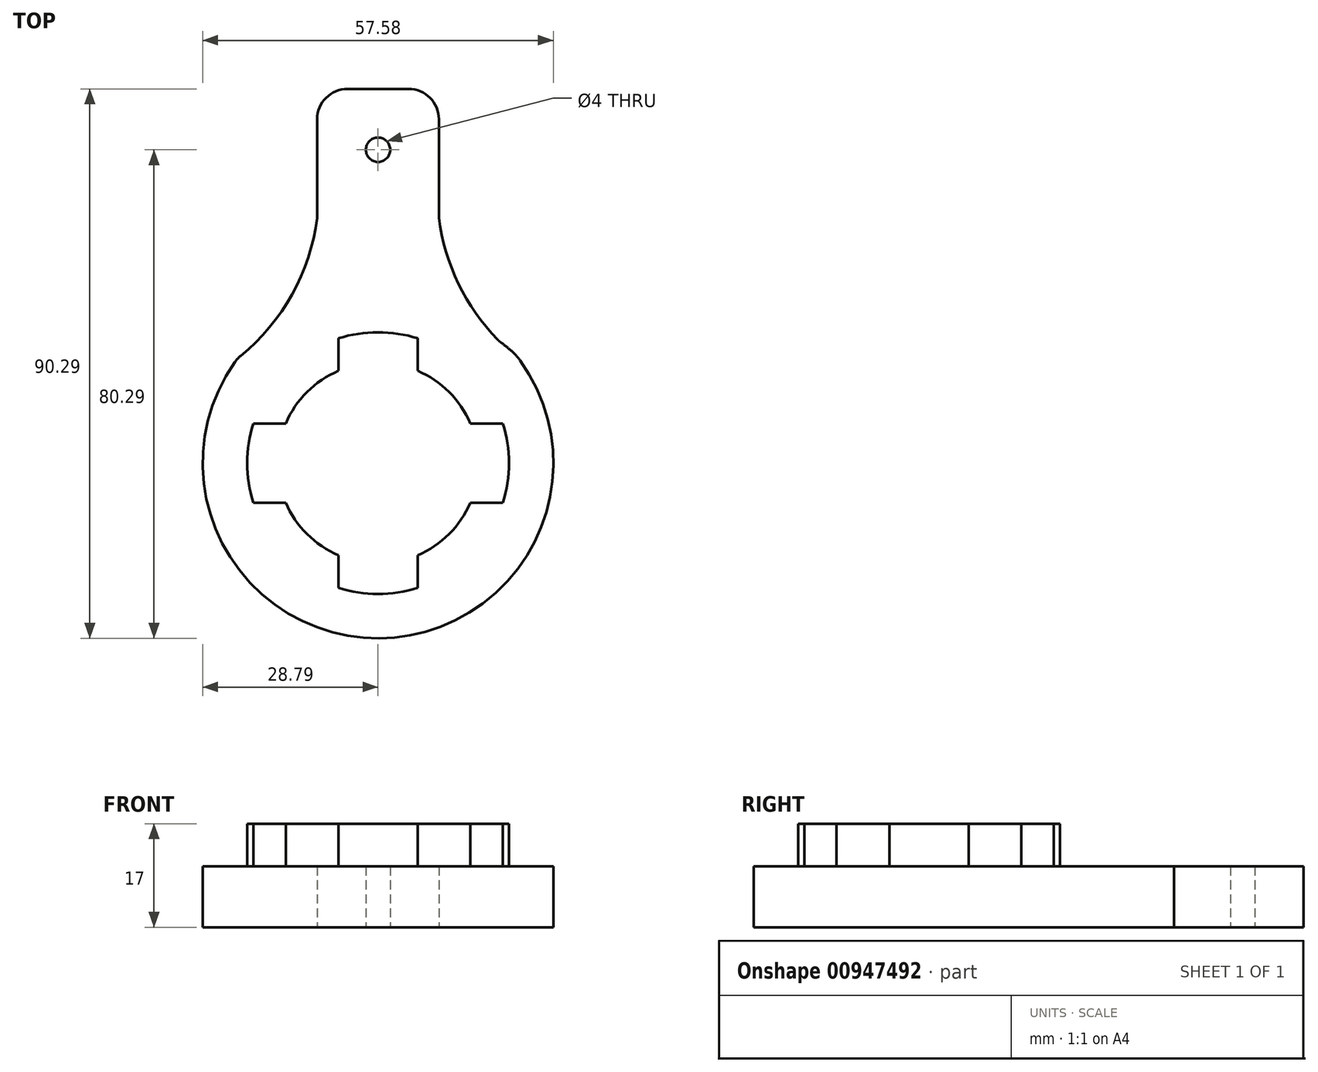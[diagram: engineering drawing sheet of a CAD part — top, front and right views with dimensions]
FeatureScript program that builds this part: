
annotation { "Feature Type Name" : "Feature", "Feature Type Description" : "" }
export const myFeature = defineFeature(function(context is Context, id is Id, definition is map)
    precondition{}
    {
        {
            var Q0;
            Q0=qCreatedBy(makeId("Top.planeOp"),FACE);
            var sketch = newSketch(context, id + "F0", { "sketchPlane" : qUnion([Q0])});
            skCircle(sketch, "E0", {"center": v(0, 0) * mm, "radius": 21.5 * mm});
            skCircle(sketch, "E1", {"center": v(0, 0) * mm, "radius": 16.5 * mm});
            skLineSegment(sketch, "E2", {"start": v(-6.5, 15.17) * mm, "end": v(-6.5, 20.5) * mm});
            skLineSegment(sketch, "E3", {"start": v(6.5, 15.17) * mm, "end": v(6.5, 20.5) * mm});
            skLineSegment(sketch, "E4", {"start": v(15.17, 6.5) * mm, "end": v(20.5, 6.5) * mm});
            skLineSegment(sketch, "E5", {"start": v(15.17, -6.5) * mm, "end": v(20.5, -6.5) * mm});
            skLineSegment(sketch, "E6", {"start": v(-15.17, 6.5) * mm, "end": v(-20.5, 6.5) * mm});
            skLineSegment(sketch, "E7", {"start": v(-15.17, -6.5) * mm, "end": v(-20.5, -6.5) * mm});
            skLineSegment(sketch, "E8", {"start": v(-6.5, -15.17) * mm, "end": v(-6.5, -20.5) * mm});
            skLineSegment(sketch, "E9", {"start": v(6.5, -15.17) * mm, "end": v(6.5, -20.5) * mm});
            skLineSegment(sketch, "E10", {"start": v(0, 61.5) * mm, "end": v(10, 61.5) * mm});
            skLineSegment(sketch, "E11", {"start": v(0, 61.5) * mm, "end": v(-10, 61.5) * mm});
            skLineSegment(sketch, "E12", {"start": v(-10, 61.5) * mm, "end": v(-10, 19.03) * mm});
            skLineSegment(sketch, "E13", {"start": v(10, 61.5) * mm, "end": v(10, 19.03) * mm});
            skArc(sketch, "E14", {"start": v(-23, 17.26) * mm, "mid": v(-14.25, 27.49) * mm, "end": v(-10, 40.27) * mm});
            skArc(sketch, "E15", {"start": v(10, 40.27) * mm, "mid": v(13.3, 29.29) * mm, "end": v(19.97, 19.97) * mm});
            skArc(sketch, "E16", {"start": v(-23, 17.26) * mm, "mid": v(-23.09, 17.18) * mm, "end": v(-23.16, 17.1) * mm});
            skArc(sketch, "E17", {"start": v(-23.16, 17.1) * mm, "mid": v(0.44, -28.79) * mm, "end": v(22.63, 17.8) * mm});
            skArc(sketch, "E18.trimOffspring", {"start": v(17.2, 23.09) * mm, "mid": v(0, 28.79) * mm, "end": v(-17.2, 23.09) * mm});
            skArc(sketch, "E19.trimOffspring", {"start": v(22.63, 17.8) * mm, "mid": v(21.34, 18.93) * mm, "end": v(19.97, 19.97) * mm});
            skLineSegment(sketch, "E20", {"start": v(0, 61.5) * mm, "end": v(0, 51.5) * mm});
            skSolve(sketch);
        }
        {
            var Q0;
            {var subQ0=sQuery(id+"F0.wireOp",EDGE,"E16");Q0=makeQuery(id+"F0.imprint","IMPRINT",FACE,{"disambiguationData":[TD([[makeQuery(id+"F0.imprint","IMPRINT",EDGE,{"derivedFrom":subQ0}),1.0]])]});}
            var Q1;
            {var subQ0=sQuery(id+"F0.wireOp",EDGE,"E2");Q1=makeQuery(id+"F0.imprint","IMPRINT",FACE,{"disambiguationData":[TD([[makeQuery(id+"F0.imprint","IMPRINT",EDGE,{"derivedFrom":subQ0}),1.0]])]});}
            var Q2;
            {var subQ0=sQuery(id+"F0.wireOp",EDGE,"E3");Q2=makeQuery(id+"F0.imprint","IMPRINT",FACE,{"disambiguationData":[TD([[makeQuery(id+"F0.imprint","IMPRINT",EDGE,{"derivedFrom":subQ0}),-1.0]])]});}
            var Q3;
            {var subQ0=sQuery(id+"F0.wireOp",EDGE,"E7");Q3=makeQuery(id+"F0.imprint","IMPRINT",FACE,{"disambiguationData":[TD([[makeQuery(id+"F0.imprint","IMPRINT",EDGE,{"derivedFrom":subQ0}),1.0]])]});}
            var Q4;
            {var subQ0=sQuery(id+"F0.wireOp",EDGE,"E5");Q4=makeQuery(id+"F0.imprint","IMPRINT",FACE,{"disambiguationData":[TD([[makeQuery(id+"F0.imprint","IMPRINT",EDGE,{"derivedFrom":subQ0}),-1.0]])]});}
            var Q5;
            {var subQ1=sQuery(id+"F0.wireOp",EDGE,"E0");var subQ8=makeQuery(id+"F0.imprint","INTERSECT",VERTEX,{"derivedFrom":[subQ1,sQuery(id+"F0.wireOp",EDGE,"E3")]});Q5=makeQuery(id+"F0.imprint","IMPRINT",FACE,{"disambiguationData":[TD([[makeQuery(id+"F0.imprint","IMPRINT",EDGE,{"disambiguationData":[TD([[subQ8,1.0]])],"derivedFrom":subQ1}),-1.0]])]});}
            var Q6;
            {var subQ0=sQuery(id+"F0.wireOp",EDGE,"E15");var subQ1=sQuery(id+"F0.wireOp",EDGE,"E13");var subQ2=makeQuery(id+"F0.imprint","INTERSECT",VERTEX,{"derivedFrom":[subQ1,subQ0]});Q6=makeQuery(id+"F0.imprint","IMPRINT",FACE,{"disambiguationData":[TD([[makeQuery(id+"F0.imprint","IMPRINT",EDGE,{"disambiguationData":[TD([[subQ2,-1.0]])],"derivedFrom":subQ1}),1.0]])]});}
            var Q7;
            {var subQ0=sQuery(id+"F0.wireOp",EDGE,"E14");var subQ1=sQuery(id+"F0.wireOp",EDGE,"E12");var subQ2=makeQuery(id+"F0.imprint","INTERSECT",VERTEX,{"derivedFrom":[subQ1,subQ0]});Q7=makeQuery(id+"F0.imprint","IMPRINT",FACE,{"disambiguationData":[TD([[makeQuery(id+"F0.imprint","IMPRINT",EDGE,{"disambiguationData":[TD([[subQ2,-1.0]])],"derivedFrom":subQ1}),-1.0]])]});}
            var Q8;
            {var subQ5=sQuery(id+"F0.wireOp",EDGE,"E10");Q8=makeQuery(id+"F0.imprint","IMPRINT",FACE,{"disambiguationData":[TD([[makeQuery(id+"F0.imprint","IMPRINT",EDGE,{"derivedFrom":subQ5}),-1.0]])]});}
            extrude(context, id + "F1", {"entities" : qUnion([Q0, Q1, Q2, Q3, Q4, Q5, Q6, Q7, Q8]), "depth" : 10 * mm, "offsetDistance" : 25 * mm});
        }
        {
            var Q0;
            {var subQ0=sQuery(id+"F0.wireOp",EDGE,"E6");Q0=makeQuery(id+"F0.imprint","IMPRINT",FACE,{"disambiguationData":[TD([[makeQuery(id+"F0.imprint","IMPRINT",EDGE,{"derivedFrom":subQ0}),1.0]])]});}
            var Q1;
            {var subQ0=sQuery(id+"F0.wireOp",EDGE,"E1");var subQ4=makeQuery(id+"F0.imprint","INTERSECT",VERTEX,{"derivedFrom":[subQ0,sQuery(id+"F0.wireOp",EDGE,"E3")]});Q1=makeQuery(id+"F0.imprint","IMPRINT",FACE,{"disambiguationData":[TD([[makeQuery(id+"F0.imprint","IMPRINT",EDGE,{"disambiguationData":[TD([[subQ4,1.0]])],"derivedFrom":subQ0}),1.0]])]});}
            var Q2;
            {var subQ0=sQuery(id+"F0.wireOp",EDGE,"E2");Q2=makeQuery(id+"F0.imprint","IMPRINT",FACE,{"disambiguationData":[TD([[makeQuery(id+"F0.imprint","IMPRINT",EDGE,{"derivedFrom":subQ0}),-1.0]])]});}
            var Q3;
            {var subQ0=sQuery(id+"F0.wireOp",EDGE,"E4");Q3=makeQuery(id+"F0.imprint","IMPRINT",FACE,{"disambiguationData":[TD([[makeQuery(id+"F0.imprint","IMPRINT",EDGE,{"derivedFrom":subQ0}),-1.0]])]});}
            var Q4;
            {var subQ0=sQuery(id+"F0.wireOp",EDGE,"E8");Q4=makeQuery(id+"F0.imprint","IMPRINT",FACE,{"disambiguationData":[TD([[makeQuery(id+"F0.imprint","IMPRINT",EDGE,{"derivedFrom":subQ0}),1.0]])]});}
            extrude(context, id + "F2", {"entities" : qUnion([Q0, Q1, Q2, Q3, Q4]), "operationType" : NewBodyOperationType.ADD, "depth" : 17 * mm, "offsetDistance" : 25 * mm});
        }
        {
            var Q0;
            Q0=makeQuery(id+"F1.opExtrude","SWEPT_EDGE",EDGE,{"disambiguationData":[OSD([sQuery(id+"F0.wireOp",EDGE,"E11"),sQuery(id+"F0.wireOp",EDGE,"E12")])]});
            var Q1;
            Q1=makeQuery(id+"F1.opExtrude","SWEPT_EDGE",EDGE,{"disambiguationData":[OSD([sQuery(id+"F0.wireOp",EDGE,"E10"),sQuery(id+"F0.wireOp",EDGE,"E13")])]});
            fillet(context, id + "F3", {"entities" : qUnion([Q0, Q1]), "radius" : 5 * mm, "tangentPropagation" : true, "allowEdgeOverflow" : false});
        }
        {
            var Q0;
            Q0=sQuery(id+"F0.wireOp",VERTEX,"E20.end");
            var Q1;
            Q1=makeQuery(id+"F1.opExtrude","SWEPT_BODY",BODY,{"disambiguationData":[OSD([sQuery(id+"F0.wireOp",EDGE,"E0"),sQuery(id+"F0.wireOp",EDGE,"E1"),sQuery(id+"F0.wireOp",EDGE,"E2"),sQuery(id+"F0.wireOp",EDGE,"E3"),sQuery(id+"F0.wireOp",EDGE,"E4"),sQuery(id+"F0.wireOp",EDGE,"E5"),sQuery(id+"F0.wireOp",EDGE,"E6"),sQuery(id+"F0.wireOp",EDGE,"E7"),sQuery(id+"F0.wireOp",EDGE,"E8"),sQuery(id+"F0.wireOp",EDGE,"E9"),sQuery(id+"F0.wireOp",EDGE,"E10"),sQuery(id+"F0.wireOp",EDGE,"E11"),sQuery(id+"F0.wireOp",EDGE,"E12"),sQuery(id+"F0.wireOp",EDGE,"E13"),sQuery(id+"F0.wireOp",EDGE,"E14"),sQuery(id+"F0.wireOp",EDGE,"E15"),sQuery(id+"F0.wireOp",EDGE,"E16"),sQuery(id+"F0.wireOp",EDGE,"E17"),sQuery(id+"F0.wireOp",EDGE,"E19.trimOffspring")])]});
            hole(context, id + "F4", {"style" : HoleStyle.SIMPLE, "endStyle" : HoleEndStyle.THROUGH, "oppositeDirection" : true, "holeDiameter" : 4 * mm, "majorDiameter" : 5 * mm, "isTappedThrough" : true, "tappedDepth" : 12 * mm, "tapClearance" : 3, "locations" : qUnion([Q0]), "scope" : qUnion([Q1])});
        }
        {
            var Q0;
            Q0=makeQuery(id+"F1.opExtrude","SWEPT_EDGE",EDGE,{"disambiguationData":[OSD([sQuery(id+"F0.wireOp",EDGE,"E17"),sQuery(id+"F0.wireOp",EDGE,"E19.trimOffspring")])]});
            var Q1;
            Q1=makeQuery(id+"F1.opExtrude","SWEPT_EDGE",EDGE,{"disambiguationData":[OSD([sQuery(id+"F0.wireOp",EDGE,"E14"),sQuery(id+"F0.wireOp",EDGE,"E16")])]});
            fillet(context, id + "F5", {"entities" : qUnion([Q0, Q1]), "radius" : 10 * mm, "tangentPropagation" : true, "allowEdgeOverflow" : false});
        }
        {
            var Q0;
            Q0=makeQuery(id+"F5.opFillet","BLEND_EDGE",EDGE,{"blendedFrom":[makeQuery(id+"F1.opExtrude","SWEPT_EDGE",EDGE,{"disambiguationData":[OSD([sQuery(id+"F0.wireOp",EDGE,"E14"),sQuery(id+"F0.wireOp",EDGE,"E16")])]}),makeQuery(id+"F1.opExtrude","SWEPT_FACE",FACE,{"disambiguationData":[OSD([sQuery(id+"F0.wireOp",EDGE,"E17")])]})],"blendedInto":[makeQuery(id+"F1.opExtrude","SWEPT_FACE",FACE,{"disambiguationData":[OSD([sQuery(id+"F0.wireOp",EDGE,"E17")])]})]});
            fillet(context, id + "F6", {"entities" : qUnion([Q0]), "radius" : 5 * mm, "tangentPropagation" : true, "allowEdgeOverflow" : false});
        }
        {
            var Q0;
            Q0=makeQuery(id+"F1.opExtrude","SWEPT_EDGE",EDGE,{"disambiguationData":[OSD([sQuery(id+"F0.wireOp",EDGE,"E15"),sQuery(id+"F0.wireOp",EDGE,"E19.trimOffspring")])]});
            fillet(context, id + "F7", {"entities" : qUnion([Q0]), "radius" : 5 * mm, "tangentPropagation" : true, "allowEdgeOverflow" : false});
        }
    });
